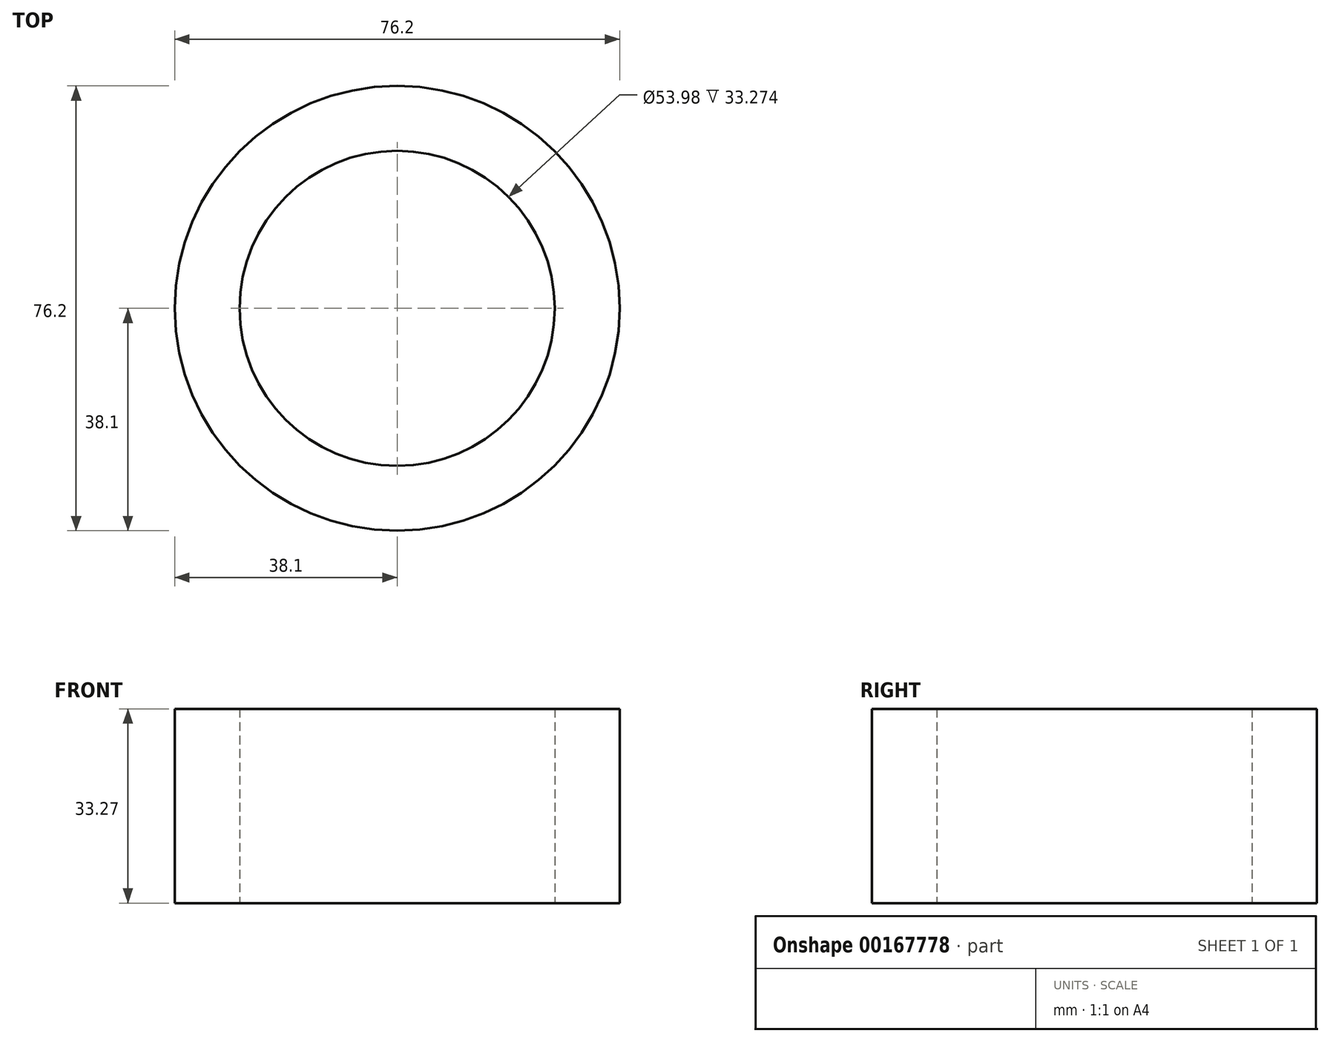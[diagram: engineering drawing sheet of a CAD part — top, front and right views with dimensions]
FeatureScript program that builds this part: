
annotation { "Feature Type Name" : "Feature", "Feature Type Description" : "" }
export const myFeature = defineFeature(function(context is Context, id is Id, definition is map)
    precondition{}
    {
        {
            var Q0;
            Q0=qCreatedBy(makeId("Top.planeOp"),FACE);
            var sketch = newSketch(context, id + "F0", { "sketchPlane" : qUnion([Q0])});
            skCircle(sketch, "E0", {"center": v(0, 0) * mm, "radius": 38.1 * mm});
            skCircle(sketch, "E1", {"center": v(0, 0) * mm, "radius": 26.99 * mm});
            skSolve(sketch);
        }
        {
            var Q0;
            Q0=makeQuery(id+"F0.imprint","IMPRINT",FACE,{"disambiguationData":[TD([[makeQuery(id+"F0.imprint","IMPRINT",EDGE,{"derivedFrom":sQuery(id+"F0.wireOp",EDGE,"E0")}),1.0]])]});
            extrude(context, id + "F1", {"entities" : qUnion([Q0]), "depth" : 33.27 * mm});
        }
    });
